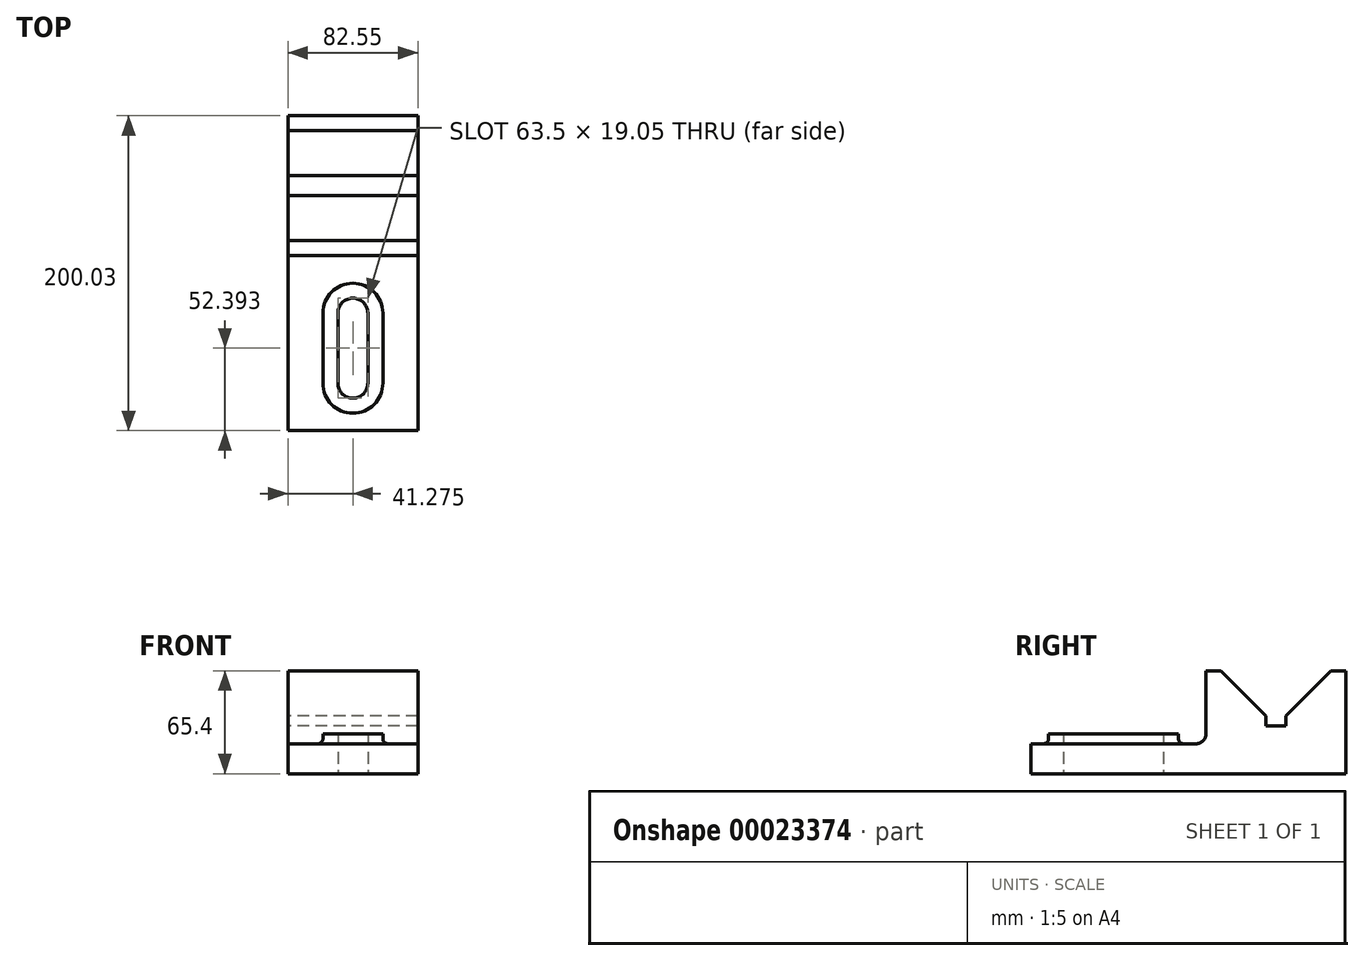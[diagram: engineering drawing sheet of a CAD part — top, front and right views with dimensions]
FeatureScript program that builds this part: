
annotation { "Feature Type Name" : "Feature", "Feature Type Description" : "" }
export const myFeature = defineFeature(function(context is Context, id is Id, definition is map)
    precondition{}
    {
        {
            var Q0;
            Q0=qCreatedBy(makeId("Right.planeOp"),FACE);
            var sketch = newSketch(context, id + "F0", { "sketchPlane" : qUnion([Q0])});
            skLineSegment(sketch, "E0.bottom", {"start": v(-95.25, 0) * mm, "end": v(-200.03, 0) * mm});
            skLineSegment(sketch, "E0.top", {"start": v(0, -19.05) * mm, "end": v(-200.03, -19.05) * mm});
            skLineSegment(sketch, "E0.left", {"start": v(0, 0) * mm, "end": v(0, -19.05) * mm});
            skLineSegment(sketch, "E0.right", {"start": v(-200.03, 0) * mm, "end": v(-200.03, -19.05) * mm});
            skLineSegment(sketch, "E1.top", {"start": v(0, 46.35) * mm, "end": v(-9.53, 46.35) * mm});
            skLineSegment(sketch, "E1.left", {"start": v(0, 0) * mm, "end": v(0, 46.35) * mm});
            skLineSegment(sketch, "E1.right", {"start": v(-88.9, 6.35) * mm, "end": v(-88.9, 46.35) * mm});
            skLineSegment(sketch, "E2", {"start": v(-9.53, 46.35) * mm, "end": v(-38.1, 17.78) * mm});
            skLineSegment(sketch, "E3", {"start": v(-79.38, 46.35) * mm, "end": v(-50.8, 17.78) * mm});
            skLineSegment(sketch, "E4", {"start": v(-50.8, 17.78) * mm, "end": v(-50.8, 11.43) * mm});
            skLineSegment(sketch, "E5", {"start": v(-38.1, 17.78) * mm, "end": v(-38.1, 11.43) * mm});
            skLineSegment(sketch, "E6", {"start": v(-38.1, 11.43) * mm, "end": v(-50.8, 11.43) * mm});
            skArc(sketch, "E7.filletArc", {"start": v(-95.25, 0) * mm, "mid": v(-90.76, 1.86) * mm, "end": v(-88.9, 6.35) * mm});
            skLineSegment(sketch, "E8.trimOffspring", {"start": v(-79.38, 46.35) * mm, "end": v(-88.9, 46.35) * mm});
            skSolve(sketch);
        }
        {
            var Q0;
            Q0=makeQuery(id+"F0.imprint","IMPRINT",FACE,{"disambiguationData":[TD([[makeQuery(id+"F0.imprint","IMPRINT",EDGE,{"derivedFrom":sQuery(id+"F0.wireOp",EDGE,"E0.bottom")}),1.0]])]});
            extrude(context, id + "F1", {"entities" : qUnion([Q0]), "depth" : 82.55 * mm});
        }
        {
            var Q0;
            Q0=makeQuery(id+"F1.opExtrude","SWEPT_FACE",FACE,{"disambiguationData":[OSD([sQuery(id+"F0.wireOp",EDGE,"E0.bottom")])]});
            var sketch = newSketch(context, id + "F2", { "sketchPlane" : qUnion([Q0])});
            skArc(sketch, "E9", {"start": v(50.8, -125.41) * mm, "mid": v(41.28, -115.89) * mm, "end": v(31.75, -125.41) * mm});
            skArc(sketch, "E10", {"start": v(31.75, -169.86) * mm, "mid": v(41.28, -179.39) * mm, "end": v(50.8, -169.86) * mm});
            skLineSegment(sketch, "E11", {"start": v(24.37, -157.75) * mm, "end": v(25.74, -157.75) * mm});
            skLineSegment(sketch, "E12.left", {"start": v(31.75, -125.41) * mm, "end": v(31.75, -169.86) * mm});
            skLineSegment(sketch, "E12.right", {"start": v(50.8, -125.41) * mm, "end": v(50.8, -169.86) * mm});
            skLineSegment(sketch, "E13.trimOffspring", {"start": v(61.1, -157.75) * mm, "end": v(62.47, -157.75) * mm});
            skArc(sketch, "E14.trimOffspring", {"start": v(60.33, -125.41) * mm, "mid": v(41.28, -106.36) * mm, "end": v(22.23, -125.41) * mm});
            skPoint(sketch, "E15.start.orphan", {"position": v(60.33, -147.64) * mm});
            skPoint(sketch, "E16.right.end.orphan", {"position": v(60.33, -169.86) * mm});
            skLineSegment(sketch, "E17.bottom", {"start": v(22.23, -125.41) * mm, "end": v(31.75, -125.41) * mm});
            skLineSegment(sketch, "E17.left", {"start": v(22.23, -125.41) * mm, "end": v(22.23, -169.86) * mm});
            skLineSegment(sketch, "E17.right", {"start": v(60.33, -125.41) * mm, "end": v(60.33, -169.86) * mm});
            skPoint(sketch, "E18.orphan", {"position": v(82.55, -147.64) * mm});
            skPoint(sketch, "E19.orphan", {"position": v(0, -147.64) * mm});
            skArc(sketch, "E20.trimOffspring", {"start": v(22.23, -169.86) * mm, "mid": v(41.28, -188.91) * mm, "end": v(60.33, -169.86) * mm});
            skPoint(sketch, "E21.orphan", {"position": v(41.28, -95.25) * mm});
            skPoint(sketch, "E22.start.orphan", {"position": v(22.23, -147.64) * mm});
            skPoint(sketch, "E23.trimOffspring.end.orphan", {"position": v(41.28, -200.03) * mm});
            skSolve(sketch);
        }
        {
            var Q0;
            Q0=makeQuery(id+"F2.imprint","IMPRINT",FACE,{"disambiguationData":[TD([[makeQuery(id+"F2.imprint","IMPRINT",EDGE,{"derivedFrom":sQuery(id+"F2.wireOp",EDGE,"E9")}),-1.0]])]});
            extrude(context, id + "F3", {"entities" : qUnion([Q0]), "operationType" : NewBodyOperationType.ADD, "depth" : 6.35 * mm});
        }
        {
            var Q0;
            Q0=makeQuery(id+"F3.opExtrude","CAP_EDGE",EDGE,{"disambiguationData":[OSD([sQuery(id+"F2.wireOp",EDGE,"E17.left")])],"isStart":true});
            fillet(context, id + "F4", {"entities" : qUnion([Q0]), "radius" : 3.17 * mm, "tangentPropagation" : true, "allowEdgeOverflow" : false});
        }
        {
            var Q0;
            Q0=makeQuery(id+"F3.boolean.opBoolean","SPLIT",FACE,{"disambiguationData":[TD([makeQuery(id+"F3.opExtrude","SWEPT_FACE",FACE,{"disambiguationData":[OSD([sQuery(id+"F2.wireOp",EDGE,"E9")])]})])],"derivedFrom":makeQuery(id+"F1.opExtrude","SWEPT_FACE",FACE,{"disambiguationData":[OSD([sQuery(id+"F0.wireOp",EDGE,"E0.bottom")])]})});
            extrude(context, id + "F5", {"entities" : qUnion([Q0]), "operationType" : NewBodyOperationType.REMOVE, "endBound" : BoundingType.THROUGH_ALL, "oppositeDirection" : true, "depth" : 25.4 * mm});
        }
    });
